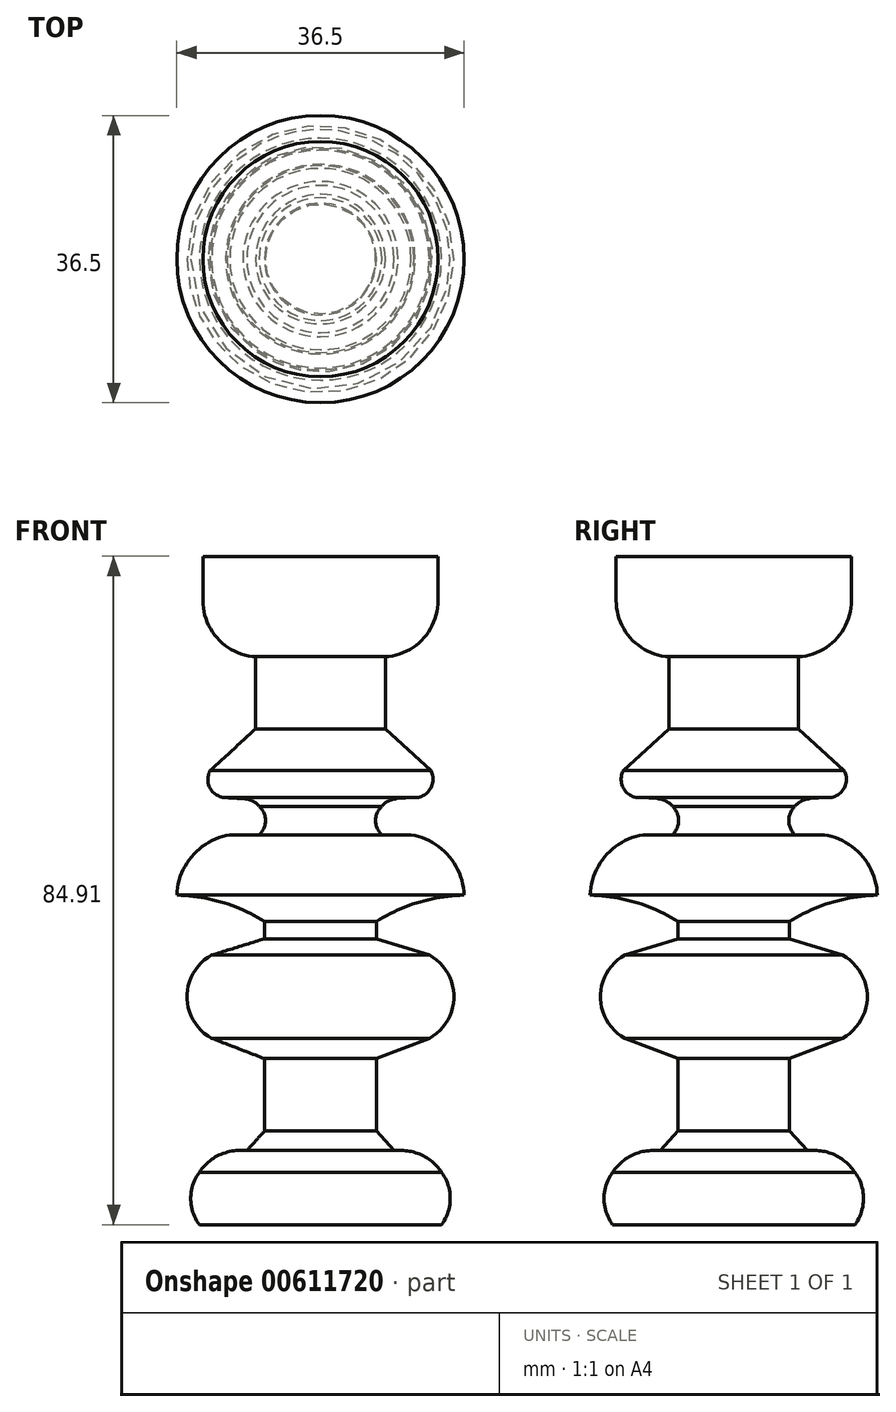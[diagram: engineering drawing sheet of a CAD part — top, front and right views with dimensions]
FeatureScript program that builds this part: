
annotation { "Feature Type Name" : "Feature", "Feature Type Description" : "" }
export const myFeature = defineFeature(function(context is Context, id is Id, definition is map)
    precondition{}
    {
        {
            var Q0;
            Q0=qCreatedBy(makeId("Front.planeOp"),FACE);
            var sketch = newSketch(context, id + "F0", { "sketchPlane" : qUnion([Q0])});
            skLineSegment(sketch, "E0", {"start": v(0, -32.98) * mm, "end": v(-15.38, -32.98) * mm});
            skArc(sketch, "E1", {"start": v(-15.38, -26.3) * mm, "mid": v(-16.49, -29.65) * mm, "end": v(-15.38, -32.98) * mm});
            skArc(sketch, "E2", {"start": v(-9.86, -23.57) * mm, "mid": v(-12.99, -24.2) * mm, "end": v(-15.38, -26.3) * mm});
            skLineSegment(sketch, "E3", {"start": v(-9.35, -23.57) * mm, "end": v(-7.1, -21.08) * mm});
            skLineSegment(sketch, "E4", {"start": v(-7.1, -21.08) * mm, "end": v(-7.1, -11.89) * mm});
            skArc(sketch, "E5", {"start": v(-13.83, 1.26) * mm, "mid": v(-16.95, -4.02) * mm, "end": v(-13.83, -9.3) * mm});
            skLineSegment(sketch, "E6", {"start": v(-13.83, -9.3) * mm, "end": v(-7.1, -11.89) * mm});
            skLineSegment(sketch, "E7", {"start": v(-13.83, 1.26) * mm, "end": v(-7.1, 3.34) * mm});
            skLineSegment(sketch, "E8", {"start": v(-7.1, 5.53) * mm, "end": v(-7.1, 3.34) * mm});
            skArc(sketch, "E9", {"start": v(-7.1, 5.53) * mm, "mid": v(-12.44, 7.97) * mm, "end": v(-18.25, 8.88) * mm});
            skArc(sketch, "E10", {"start": v(-11.52, 16.55) * mm, "mid": v(-16.24, 13.9) * mm, "end": v(-18.25, 8.88) * mm});
            skLineSegment(sketch, "E11", {"start": v(-7.79, 16.55) * mm, "end": v(-11.52, 16.55) * mm});
            skArc(sketch, "E12", {"start": v(-7.79, 16.55) * mm, "mid": v(-7, 18.37) * mm, "end": v(-7.79, 20.18) * mm});
            skArc(sketch, "E13", {"start": v(-7.79, 20.18) * mm, "mid": v(-8.66, 20.86) * mm, "end": v(-9.73, 21.15) * mm});
            skLineSegment(sketch, "E14", {"start": v(-9.73, 21.15) * mm, "end": v(-11.85, 21.26) * mm});
            skArc(sketch, "E15", {"start": v(-14.03, 24.7) * mm, "mid": v(-13.99, 22.43) * mm, "end": v(-12.04, 21.26) * mm});
            skLineSegment(sketch, "E16", {"start": v(-14.03, 24.7) * mm, "end": v(-8.23, 30) * mm});
            skLineSegment(sketch, "E17", {"start": v(-8.23, 30) * mm, "end": v(-8.23, 36.72) * mm});
            skLineSegment(sketch, "E18", {"start": v(-8.23, 36.72) * mm, "end": v(-8.23, 39.17) * mm});
            skLineSegment(sketch, "E19", {"start": v(-14.94, 46.3) * mm, "end": v(-14.94, 51.93) * mm});
            skArc(sketch, "E20", {"start": v(-14.94, 46.3) * mm, "mid": v(-13, 41.4) * mm, "end": v(-8.23, 39.17) * mm});
            skLineSegment(sketch, "E21", {"start": v(-14.94, 51.93) * mm, "end": v(0, 51.93) * mm});
            skLineSegment(sketch, "E22", {"start": v(0, 51.93) * mm, "end": v(0, -32.98) * mm});
            skLineSegment(sketch, "E23", {"start": v(-9.86, -23.57) * mm, "end": v(-9.35, -23.57) * mm});
            skLineSegment(sketch, "E24", {"start": v(-12.04, 21.26) * mm, "end": v(-11.85, 21.26) * mm});
            skSolve(sketch);
        }
        {
            var Q0;
            Q0 = qSketchRegion(id + "F0", true);
            var Q1;
            Q1=sQuery(id+"F0.wireOp",EDGE,"E24");
            var Q2;
            Q2=sQuery(id+"F0.wireOp",EDGE,"E15");
            var Q3;
            Q3=sQuery(id+"F0.wireOp",EDGE,"E14");
            var Q4;
            Q4=sQuery(id+"F0.wireOp",EDGE,"E16");
            var Q5;
            Q5=sQuery(id+"F0.wireOp",EDGE,"E17");
            var Q6;
            Q6=sQuery(id+"F0.wireOp",EDGE,"E18");
            var Q7;
            Q7=sQuery(id+"F0.wireOp",EDGE,"E20");
            var Q8;
            Q8=sQuery(id+"F0.wireOp",EDGE,"E19");
            var Q9;
            Q9=sQuery(id+"F0.wireOp",EDGE,"E21");
            var Q10;
            Q10=sQuery(id+"F0.wireOp",EDGE,"E13");
            var Q11;
            Q11=sQuery(id+"F0.wireOp",EDGE,"E12");
            var Q12;
            Q12=sQuery(id+"F0.wireOp",EDGE,"E11");
            var Q13;
            Q13=sQuery(id+"F0.wireOp",EDGE,"E10");
            var Q14;
            Q14=sQuery(id+"F0.wireOp",EDGE,"E9");
            var Q15;
            Q15=sQuery(id+"F0.wireOp",EDGE,"E8");
            var Q16;
            Q16=sQuery(id+"F0.wireOp",EDGE,"E7");
            var Q17;
            Q17=sQuery(id+"F0.wireOp",EDGE,"E5");
            var Q18;
            Q18=sQuery(id+"F0.wireOp",EDGE,"E6");
            var Q19;
            Q19=sQuery(id+"F0.wireOp",EDGE,"E4");
            var Q20;
            Q20=sQuery(id+"F0.wireOp",EDGE,"E0");
            var Q21;
            Q21=sQuery(id+"F0.wireOp",EDGE,"E1");
            var Q22;
            Q22=sQuery(id+"F0.wireOp",EDGE,"E2");
            var Q23;
            Q23=sQuery(id+"F0.wireOp",EDGE,"E23");
            var Q24;
            Q24=sQuery(id+"F0.wireOp",EDGE,"E3");
            var Q25;
            Q25=sQuery(id+"F0.wireOp",EDGE,"E22");
            revolve(context, id + "F1", {"bodyType" : ToolBodyType.SURFACE, "entities" : qUnion([Q0]), "surfaceEntities" : qUnion([Q1, Q2, Q3, Q4, Q5, Q6, Q7, Q8, Q9, Q10, Q11, Q12, Q13, Q14, Q15, Q16, Q17, Q18, Q19, Q20, Q21, Q22, Q23, Q24]), "axis" : qUnion([Q25]), "revolveType" : RevolveType.FULL});
        }
    });
